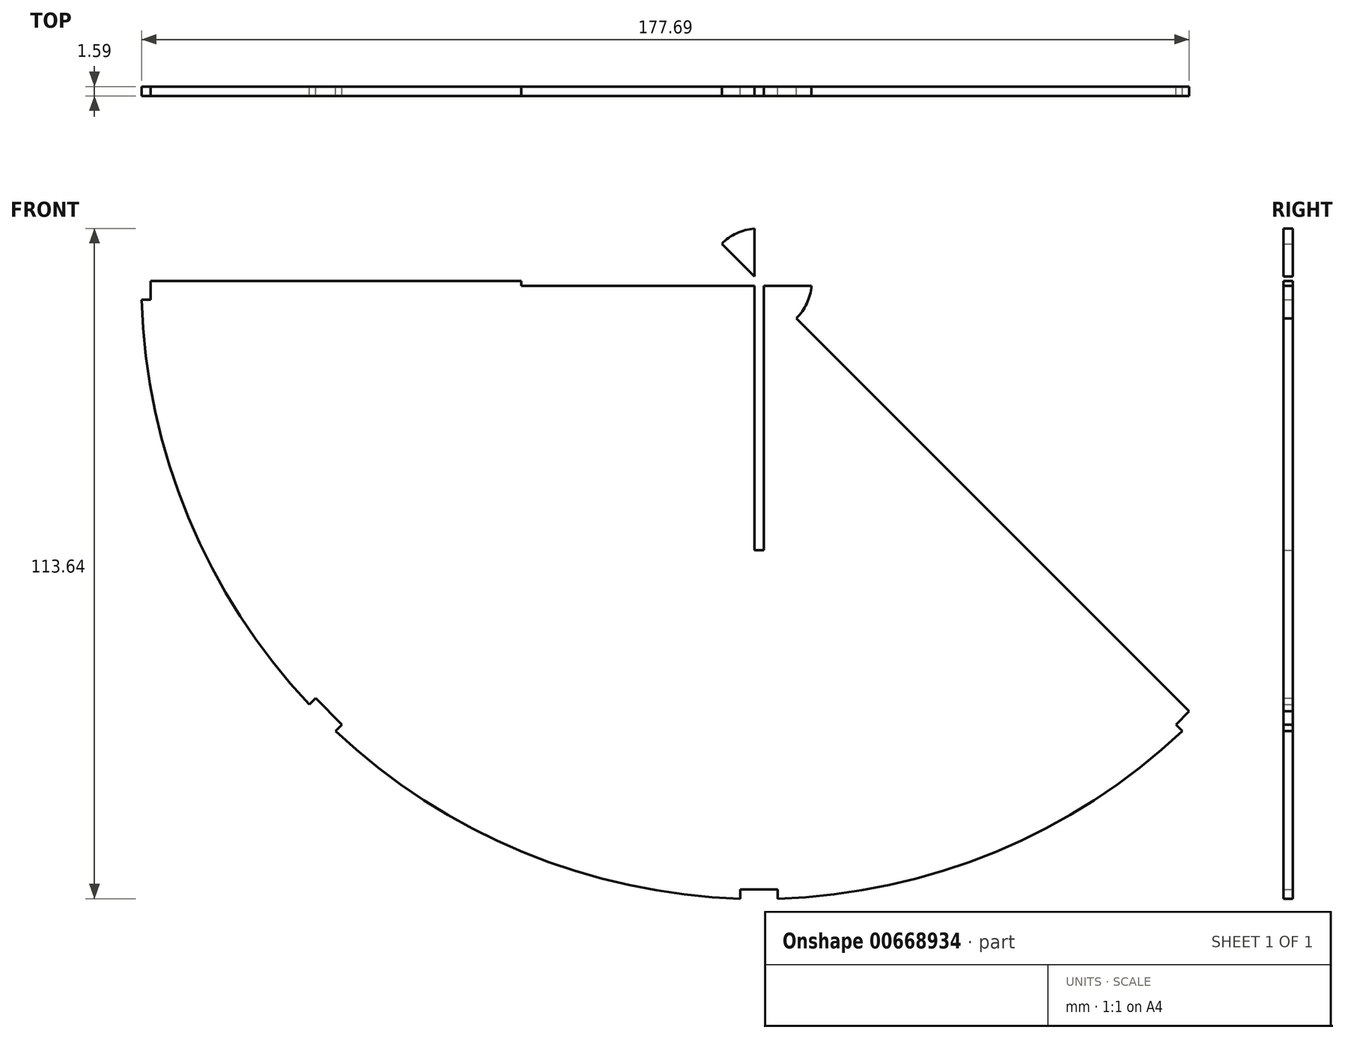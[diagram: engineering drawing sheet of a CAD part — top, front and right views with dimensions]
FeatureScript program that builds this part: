
annotation { "Feature Type Name" : "Feature", "Feature Type Description" : "" }
export const myFeature = defineFeature(function(context is Context, id is Id, definition is map)
    precondition{}
    {
        {
            var Q0;
            Q0=qCreatedBy(makeId("Front.planeOp"),FACE);
            var sketch = newSketch(context, id + "F0", { "sketchPlane" : qUnion([Q0])});
            skCircle(sketch, "E0", {"center": v(0, 0) * mm, "radius": 104.78 * mm});
            skLineSegment(sketch, "E1", {"start": v(0, 103.19) * mm, "end": v(3.18, 103.19) * mm});
            skLineSegment(sketch, "E2", {"start": v(0, -103.17) * mm, "end": v(3.18, -103.17) * mm});
            skLineSegment(sketch, "E3", {"start": v(103.19, 0) * mm, "end": v(103.19, -3.18) * mm});
            skLineSegment(sketch, "E4", {"start": v(-103.19, 0) * mm, "end": v(-103.19, -3.17) * mm});
            skLineSegment(sketch, "E5", {"start": v(74.09, -74.09) * mm, "end": v(-74.09, 74.09) * mm});
            skLineSegment(sketch, "E6", {"start": v(-74.09, -74.09) * mm, "end": v(74.09, 74.09) * mm});
            skLineSegment(sketch, "E7", {"start": v(-75.2, 70.72) * mm, "end": v(-72.96, 72.96) * mm});
            skLineSegment(sketch, "E8", {"start": v(-72.96, -72.96) * mm, "end": v(-75.2, -70.72) * mm});
            skLineSegment(sketch, "E9", {"start": v(72.96, -72.96) * mm, "end": v(70.72, -75.2) * mm});
            skLineSegment(sketch, "E10.MirrorCS", {"start": v(-72.96, -72.96) * mm, "end": v(-70.72, -75.2) * mm});
            skLineSegment(sketch, "E11", {"start": v(-75.2, -70.72) * mm, "end": v(-76.3, -71.8) * mm});
            skLineSegment(sketch, "E12", {"start": v(-70.72, -75.2) * mm, "end": v(-71.8, -76.3) * mm});
            skLineSegment(sketch, "E13", {"start": v(-103.19, -3.18) * mm, "end": v(-104.73, -3.18) * mm});
            skLineSegment(sketch, "E14.MirrorCS", {"start": v(-103.19, 0) * mm, "end": v(-103.19, 3.17) * mm});
            skLineSegment(sketch, "E15", {"start": v(-103.19, 3.18) * mm, "end": v(-104.73, 3.18) * mm});
            skLineSegment(sketch, "E16.MirrorCS", {"start": v(72.96, -72.96) * mm, "end": v(75.2, -70.72) * mm});
            skLineSegment(sketch, "E17", {"start": v(33.68, -38.17) * mm, "end": v(70.72, -75.2) * mm});
            skLineSegment(sketch, "E18", {"start": v(103.19, -3.17) * mm, "end": v(104.73, -3.17) * mm});
            skLineSegment(sketch, "E19", {"start": v(75.2, -70.72) * mm, "end": v(76.3, -71.8) * mm});
            skLineSegment(sketch, "E20", {"start": v(3.18, -103.17) * mm, "end": v(3.18, -104.73) * mm});
            skLineSegment(sketch, "E21", {"start": v(-5.76, -104.3) * mm, "end": v(-5.76, -104.62) * mm});
            skLineSegment(sketch, "E22.MirrorCS", {"start": v(0, 103.19) * mm, "end": v(-3.18, 103.19) * mm});
            skLineSegment(sketch, "E23", {"start": v(-3.18, 103.19) * mm, "end": v(-3.18, 104.73) * mm});
            skLineSegment(sketch, "E24", {"start": v(3.18, 103.19) * mm, "end": v(3.18, 104.73) * mm});
            skLineSegment(sketch, "E25.MirrorCS", {"start": v(-70.72, 75.2) * mm, "end": v(-72.96, 72.96) * mm});
            skLineSegment(sketch, "E26", {"start": v(-75.2, 70.72) * mm, "end": v(-76.3, 71.8) * mm});
            skLineSegment(sketch, "E27", {"start": v(-70.72, 75.2) * mm, "end": v(-71.8, 76.3) * mm});
            skLineSegment(sketch, "E28", {"start": v(70.72, -75.2) * mm, "end": v(71.8, -76.3) * mm});
            skLineSegment(sketch, "E29.MirrorCS", {"start": v(103.19, 0) * mm, "end": v(103.19, 3.18) * mm});
            skLineSegment(sketch, "E30.MirrorCS", {"start": v(103.19, 3.17) * mm, "end": v(104.73, 3.17) * mm});
            skLineSegment(sketch, "E31.MirrorCS", {"start": v(0, -103.17) * mm, "end": v(-3.18, -103.17) * mm});
            skLineSegment(sketch, "E32.MirrorCS", {"start": v(-3.18, -103.17) * mm, "end": v(-3.18, -104.73) * mm});
            skLineSegment(sketch, "E33", {"start": v(72.93, 72.93) * mm, "end": v(75.18, 70.68) * mm});
            skLineSegment(sketch, "E34", {"start": v(75.18, 70.68) * mm, "end": v(76.3, 71.8) * mm});
            skLineSegment(sketch, "E35.MirrorCS", {"start": v(72.93, 72.93) * mm, "end": v(70.68, 75.18) * mm});
            skLineSegment(sketch, "E36.MirrorCS", {"start": v(70.68, 75.18) * mm, "end": v(71.8, 76.3) * mm});
            skLineSegment(sketch, "E37.bottom", {"start": v(-0.8, 45.64) * mm, "end": v(0.8, 45.64) * mm});
            skLineSegment(sketch, "E37.top", {"start": v(-0.8, -45.64) * mm, "end": v(0.8, -45.64) * mm});
            skLineSegment(sketch, "E37.left", {"start": v(-0.8, 45.64) * mm, "end": v(-0.8, -45.64) * mm});
            skLineSegment(sketch, "E37.right", {"start": v(0.8, 45.64) * mm, "end": v(0.8, -45.64) * mm});
            skLineSegment(sketch, "E38.bottom", {"start": v(40.34, -0.8) * mm, "end": v(-40.34, -0.8) * mm});
            skLineSegment(sketch, "E38.top", {"start": v(40.34, 0.8) * mm, "end": v(-40.34, 0.8) * mm});
            skLineSegment(sketch, "E38.left", {"start": v(40.34, -0.8) * mm, "end": v(40.34, 0.8) * mm});
            skLineSegment(sketch, "E38.right", {"start": v(-40.34, -0.8) * mm, "end": v(-40.34, 0.8) * mm});
            skCircle(sketch, "E39", {"center": v(0, 0) * mm, "radius": 8.95 * mm});
            skLineSegment(sketch, "E40", {"start": v(3.18, -104.73) * mm, "end": v(3.18, -103.17) * mm});
            skLineSegment(sketch, "E41", {"start": v(0, 0) * mm, "end": v(-132.64, 0) * mm});
            skLineSegment(sketch, "E42", {"start": v(0, 0) * mm, "end": v(155, 0) * mm});
            skSolve(sketch);
        }
        {
            var Q0;
            Q0=makeQuery(id+"F0.imprint","IMPRINT",FACE,{"disambiguationData":[TD([[makeQuery(id+"F0.imprint","IMPRINT",EDGE,{"derivedFrom":sQuery(id+"F0.wireOp",EDGE,"E2")}),1.0]])]});
            var Q1;
            Q1=makeQuery(id+"F0.imprint","IMPRINT",FACE,{"disambiguationData":[TD([[makeQuery(id+"F0.imprint","IMPRINT",EDGE,{"derivedFrom":sQuery(id+"F0.wireOp",EDGE,"E4")}),1.0]])]});
            var Q2;
            {var subQ0=sQuery(id+"F0.wireOp",EDGE,"E39");var subQ1=sQuery(id+"F0.wireOp",EDGE,"E6");var subQ2=makeQuery(id+"F0.imprint","INTERSECT",VERTEX,{"disambiguationData":[OD(0.0)],"derivedFrom":[subQ1,subQ0]});Q2=makeQuery(id+"F0.imprint","IMPRINT",FACE,{"disambiguationData":[TD([[makeQuery(id+"F0.imprint","IMPRINT",EDGE,{"disambiguationData":[TD([[subQ2,1.0]])],"derivedFrom":subQ0}),1.0]])]});}
            var Q3;
            {var subQ0=sQuery(id+"F0.wireOp",EDGE,"E39");var subQ1=sQuery(id+"F0.wireOp",EDGE,"E6");var subQ2=makeQuery(id+"F0.imprint","INTERSECT",VERTEX,{"disambiguationData":[OD(0.0)],"derivedFrom":[subQ1,subQ0]});Q3=makeQuery(id+"F0.imprint","IMPRINT",FACE,{"disambiguationData":[TD([[makeQuery(id+"F0.imprint","IMPRINT",EDGE,{"disambiguationData":[TD([[subQ2,-1.0]])],"derivedFrom":subQ0}),1.0]])]});}
            var Q4;
            {var subQ0=sQuery(id+"F0.wireOp",EDGE,"E39");var subQ1=sQuery(id+"F0.wireOp",EDGE,"E5");var subQ2=makeQuery(id+"F0.imprint","INTERSECT",VERTEX,{"disambiguationData":[OD(0.0)],"derivedFrom":[subQ1,subQ0]});Q4=makeQuery(id+"F0.imprint","IMPRINT",FACE,{"disambiguationData":[TD([[makeQuery(id+"F0.imprint","IMPRINT",EDGE,{"disambiguationData":[TD([[subQ2,1.0]])],"derivedFrom":subQ0}),1.0]])]});}
            var Q5;
            {var subQ0=sQuery(id+"F0.wireOp",EDGE,"E39");var subQ1=sQuery(id+"F0.wireOp",EDGE,"E37.left");var subQ2=makeQuery(id+"F0.imprint","INTERSECT",VERTEX,{"disambiguationData":[OD(1.0)],"derivedFrom":[subQ1,subQ0]});Q5=makeQuery(id+"F0.imprint","IMPRINT",FACE,{"disambiguationData":[TD([[makeQuery(id+"F0.imprint","IMPRINT",EDGE,{"disambiguationData":[TD([[subQ2,-1.0]])],"derivedFrom":subQ0}),1.0]])]});}
            var Q6;
            {var subQ0=sQuery(id+"F0.wireOp",EDGE,"E38.bottom");var subQ5=sQuery(id+"F0.wireOp",EDGE,"E39");var subQ6=makeQuery(id+"F0.imprint","INTERSECT",VERTEX,{"disambiguationData":[OD(0.0)],"derivedFrom":[subQ0,subQ5]});Q6=makeQuery(id+"F0.imprint","IMPRINT",FACE,{"disambiguationData":[TD([[makeQuery(id+"F0.imprint","IMPRINT",EDGE,{"disambiguationData":[TD([[subQ6,-1.0]])],"derivedFrom":subQ5}),1.0]])]});}
            var Q7;
            {var subQ3=sQuery(id+"F0.wireOp",EDGE,"E38.bottom");var subQ5=sQuery(id+"F0.wireOp",EDGE,"E39");var subQ6=makeQuery(id+"F0.imprint","INTERSECT",VERTEX,{"disambiguationData":[OD(1.0)],"derivedFrom":[subQ3,subQ5]});Q7=makeQuery(id+"F0.imprint","IMPRINT",FACE,{"disambiguationData":[TD([[makeQuery(id+"F0.imprint","IMPRINT",EDGE,{"disambiguationData":[TD([[subQ6,1.0]])],"derivedFrom":subQ5}),1.0]])]});}
            extrude(context, id + "F1", {"entities" : qUnion([Q0, Q1, Q2, Q3, Q4, Q5, Q6, Q7]), "depth" : 1.59 * mm, "offsetDistance" : 25.4 * mm});
        }
    });
